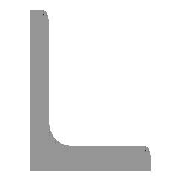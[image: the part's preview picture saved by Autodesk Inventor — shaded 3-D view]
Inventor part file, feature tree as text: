
AUTODESK INVENTOR PART (.ipt)
format: ipt  version: 2024.1 (Build 281209000, 209)  size: 120,320 bytes
history: native  units: mm (DEFAULTED — no unit token found)
features: other x4, sketch x1, plane x1
ambient origin geometry x8: Origin, YZ Plane, XZ Plane, XY Plane, X Axis, Y Axis, Z Axis, Center Point
bodies: Solid1 (feature_tree), Body (feature_tree)
feature tree (6):
  parser-record x1  (decoder bookkeeping rows leaked as tree rows — omitted from the tree; the rows remain in map.json)
  other  "Driven Length"
  other  "Start Plane"
  other  "End Plane"
  sketch  "Sketch3"  dims[d0=28.702mm d1=28.702mm d2=3.175mm d3=3.175mm d4=960.0mm d5=0.0mm d10=0.0mm d11=0.0mm d12=-0.0mm d13=960.0mm d14=2.286mm d15=1.27mm d16=90.0deg d17=960.0mm]
  plane  "Work Plane3"
